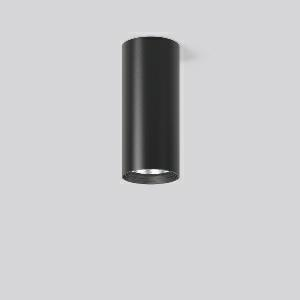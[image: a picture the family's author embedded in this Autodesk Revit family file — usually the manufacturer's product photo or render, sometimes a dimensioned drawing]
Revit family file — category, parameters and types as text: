
# Revit family: heledon_mini_a_931200_003_2_9853
name_source: partatom
category: Lighting Fixtures
units: mm (PartAtom-declared; Revit-internal decimal feet)

## family parameters
Cut with Voids When Loaded = No
Host = Face
Light Source = No
Part Type = Normal
Room Calculation Point = No
Round Connector Dimension = Use Diameter
Shared = No

## types (1)
- HELEDON mini A (1 x LED Modul 927, 2400 lm, 2700)
    Apparent Load = 20 VA
    Approval mark = CE
    CIE Flux Codes = 100 100 100 100 100
    Color Rendering = 92
    Color Temperature = 2700
    Default Elevation = 1800 mm
    Description = Series: HELEDON mini
Cylindrical surface-mounted downlight. Housing: die-cast aluminium, powder-coated. Internal ceiling frame polycarbonate with bayonet mounting. Black plastic ring and recessed LED to prevent glare from the side. Optical assembly with reflector made of MIRO-Silver with 98% total light reflection for outstanding efficiency - can be changed without tools. Best colour rendering index Ra>90. Suitable for Ceiling mounting. Easy installation with a separate ceiling frame with bayonet mounting and plug connection. Driver integrated. Connected via plug-in connector. High quality converter without flickering and stroboscopic effect. The following accessories can be mounted without use of tools: interchangeable lenses, decorative glasses, honeycomb louvre, clear and frosted diffusers, white interchangeable plastic ring. 
Colour: deep black, matt (RAL 9005)
Diameter: 87 mm
Height: 197 mm
Lamp: LED
Socket: without socket
Colour temperature: 2700K
Colour rendering index (CRI): 92
System power: 20 W
Rated luminous flux: 2400 lm
Luminous efficiency: 120 lm/W
Control gear: Regulated power supply
Protection class: I
Type of protection: IP 20
    Height = 197 mm
    Lamp = 1 x LED Modul 927
    Lamp Light Flux = 2400 lm
    Lamp count = 1
    Length = 87 mm
    Lifetime = 50000 h
    Luminous efficacy = 120 lm/W
    Manufacturer = RZB
    ModVariant = No
    Model = 931200.003.2
    Mounting Place = Ceiling
    Mounting Type = Surface mounted
    Number of Poles = 1
    OnlyDefault = Yes
    Power Factor = 1
    Product Name = HELEDON mini A
    Product group = Surface mounted downlights
    ProductGroupID = 302
    Protection Class = Protection class I
    Protection Degree = IP 20
    RLX_Detail_Level = 1
    RLX_Emergency_Light_Flux = 0 lm
    RLX_Emergency_Type = 0
    RLX_Emergency_Type_DB = No
    RlxData = <blob elided: 106489 chars, md5=4f5d9cee>
    Socket = socket
    Standby Power = 0 W
    System Light Flux = 2400 lm
    System Power = 20 W
    Type Comments = Product without accessories
    Type Image = 931188.003.jpg
    URL = http://relux.com
    VarID = ---
    Voltage = 230 V
    Voltage Range = 220-240 V
    Weight = 0.00 kg
    Width = 0 mm  [stored 0 ft]

note: [stored X ft] marks values corroborated as IEEE doubles in the binary element streams (Revit-internal decimal feet)

## geometry (parser evidence)
native form markers: Blend x4, Sweep x9
no freeform markers — native parametric forms only
